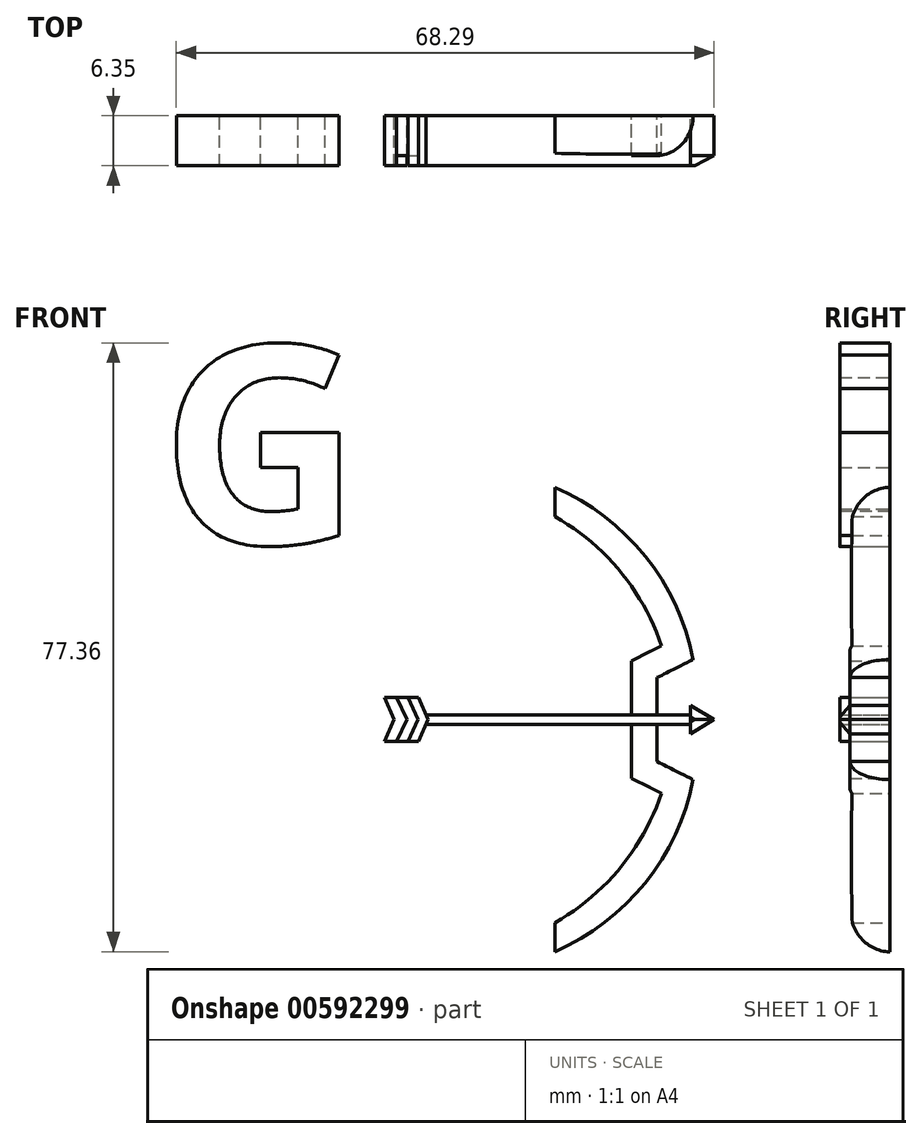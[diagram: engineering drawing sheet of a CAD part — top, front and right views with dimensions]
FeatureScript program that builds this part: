
annotation { "Feature Type Name" : "Feature", "Feature Type Description" : "" }
export const myFeature = defineFeature(function(context is Context, id is Id, definition is map)
    precondition{}
    {
        {
            var Q0;
            Q0=qCreatedBy(makeId("Front.planeOp"),FACE);
            var sketch = newSketch(context, id + "F0", { "sketchPlane" : qUnion([Q0])});
            skText(sketch, "E0", { "text": "G", "fontName": "OpenSans-Bold.ttf"});
            skArc(sketch, "E1", {"start": v(24.9, 7.63) * mm, "mid": v(18.82, 20.73) * mm, "end": v(7.34, 29.5) * mm});
            skLineSegment(sketch, "E2", {"start": v(24.9, 7.63) * mm, "end": v(20.3, 5.32) * mm});
            skLineSegment(sketch, "E3", {"start": v(20.3, 5.32) * mm, "end": v(20.3, 0.62) * mm});
            skArc(sketch, "E4", {"start": v(20.87, 9.35) * mm, "mid": v(15.63, 18.83) * mm, "end": v(7.34, 25.8) * mm});
            skLineSegment(sketch, "E5", {"start": v(7.34, 25.8) * mm, "end": v(-10.9, 2.79) * mm});
            skLineSegment(sketch, "E6", {"start": v(7.34, 29.5) * mm, "end": v(7.34, 25.8) * mm});
            skLineSegment(sketch, "E7", {"start": v(20.87, 9.35) * mm, "end": v(17.07, 7.46) * mm});
            skLineSegment(sketch, "E8", {"start": v(17.07, 7.46) * mm, "end": v(17.07, 0.62) * mm});
            skLineSegment(sketch, "E9.MirrorCS", {"start": v(20.3, -5.32) * mm, "end": v(20.3, -0.62) * mm});
            skLineSegment(sketch, "E10.MirrorCS", {"start": v(17.07, -7.46) * mm, "end": v(17.07, -0.62) * mm});
            skLineSegment(sketch, "E11.MirrorCS", {"start": v(20.87, -9.35) * mm, "end": v(17.07, -7.46) * mm});
            skLineSegment(sketch, "E12.MirrorCS", {"start": v(24.9, -7.63) * mm, "end": v(20.3, -5.32) * mm});
            skArc(sketch, "E13.MirrorCS", {"start": v(24.9, -7.63) * mm, "mid": v(18.82, -20.73) * mm, "end": v(7.34, -29.5) * mm});
            skArc(sketch, "E14.MirrorCS", {"start": v(20.87, -9.35) * mm, "mid": v(15.63, -18.83) * mm, "end": v(7.34, -25.8) * mm});
            skLineSegment(sketch, "E15.MirrorCS", {"start": v(7.34, -29.5) * mm, "end": v(7.34, -25.8) * mm});
            skLineSegment(sketch, "E16.MirrorCS", {"start": v(7.34, -25.8) * mm, "end": v(-10.9, -2.79) * mm});
            skLineSegment(sketch, "E17", {"start": v(-14.33, 2.79) * mm, "end": v(-13.11, 0) * mm});
            skLineSegment(sketch, "E18", {"start": v(-13.11, 0) * mm, "end": v(-8.8, 0) * mm});
            skLineSegment(sketch, "E19", {"start": v(-8.8, 0) * mm, "end": v(-10.01, 2.79) * mm});
            skLineSegment(sketch, "E20", {"start": v(-14.33, 2.79) * mm, "end": v(-10.01, 2.79) * mm});
            skLineSegment(sketch, "E21", {"start": v(-9.06, 0.62) * mm, "end": v(24.54, 0.62) * mm});
            skLineSegment(sketch, "E22", {"start": v(24.54, 0.62) * mm, "end": v(24.54, 1.82) * mm});
            skLineSegment(sketch, "E23", {"start": v(24.54, 1.82) * mm, "end": v(27.54, 0) * mm});
            skLineSegment(sketch, "E24", {"start": v(24.54, 0.62) * mm, "end": v(24.54, 0) * mm});
            skLineSegment(sketch, "E25", {"start": v(-11.33, 2.79) * mm, "end": v(-10.04, 0) * mm});
            skLineSegment(sketch, "E26", {"start": v(-12.8, 2.79) * mm, "end": v(-11.48, 0) * mm});
            skLineSegment(sketch, "E27.MirrorCS", {"start": v(-14.33, -2.79) * mm, "end": v(-13.11, 0) * mm});
            skLineSegment(sketch, "E28.MirrorCS", {"start": v(-14.33, -2.79) * mm, "end": v(-10.01, -2.79) * mm});
            skLineSegment(sketch, "E29.MirrorCS", {"start": v(-12.8, -2.79) * mm, "end": v(-11.48, 0) * mm});
            skLineSegment(sketch, "E30.MirrorCS", {"start": v(-11.33, -2.79) * mm, "end": v(-10.04, 0) * mm});
            skLineSegment(sketch, "E31.MirrorCS", {"start": v(-8.8, 0) * mm, "end": v(-10.01, -2.79) * mm});
            skLineSegment(sketch, "E32.MirrorCS", {"start": v(-9.06, -0.62) * mm, "end": v(24.54, -0.62) * mm});
            skLineSegment(sketch, "E33.MirrorCS", {"start": v(24.54, -1.82) * mm, "end": v(27.54, 0) * mm});
            skLineSegment(sketch, "E34.MirrorCS", {"start": v(24.54, -0.62) * mm, "end": v(24.54, -1.82) * mm});
            skLineSegment(sketch, "E35.MirrorCS", {"start": v(24.54, -0.62) * mm, "end": v(24.54, 0) * mm});
            skPoint(sketch, "E36.orphan", {"position": v(17.07, 0) * mm});
            skPoint(sketch, "E37.orphan", {"position": v(20.3, 0) * mm});
            skPoint(sketch, "E38.orphan", {"position": v(-13.11, 0) * mm});
            const initialGuessF0  = {"E0": [-0.0428, 0.02232, 1, 0, 0.0254]};
            skSetInitialGuess(sketch, initialGuessF0);
            skSolve(sketch);
        }
        {
            var Q0;
            Q0=makeQuery(id+"F0.imprint","IMPRINT",FACE,{"disambiguationData":[TD([[makeQuery(id+"F0.imprint","IMPRINT",EDGE,{"derivedFrom":sQuery(id+"F0.wireOp",EDGE,"E1")}),1.0]])]});
            var Q1;
            {var subQ1=sQuery(id+"F0.wireOp",EDGE,"E9.MirrorCS");Q1=makeQuery(id+"F0.imprint","IMPRINT",FACE,{"disambiguationData":[TD([[makeQuery(id+"F0.imprint","IMPRINT",EDGE,{"derivedFrom":subQ1}),1.0]])]});}
            var Q2;
            Q2=sQuery(id+"F0.wireOp",EDGE,"E5");
            var Q3;
            Q3=sQuery(id+"F0.wireOp",EDGE,"E16.MirrorCS");
            extrude(context, id + "F1", {"entities" : qUnion([Q0, Q1]), "bodyType" : ToolBodyType.SURFACE, "surfaceEntities" : qUnion([Q2, Q3]), "depth" : 5.08 * mm, "offsetDistance" : 25.4 * mm});
        }
        {
            var Q0;
            Q0=makeQuery(id+"F0.imprint","IMPRINT",FACE,{"disambiguationData":[TD([[makeQuery(id+"F0.imprint","IMPRINT",EDGE,{"derivedFrom":sQuery(id+"F0.wireOp",EDGE,"E1")}),1.0]])]});
            var Q1;
            {var subQ1=sQuery(id+"F0.wireOp",EDGE,"E9.MirrorCS");Q1=makeQuery(id+"F0.imprint","IMPRINT",FACE,{"disambiguationData":[TD([[makeQuery(id+"F0.imprint","IMPRINT",EDGE,{"derivedFrom":subQ1}),1.0]])]});}
            var Q2;
            {var subQ0=sQuery(id+"F0.wireOp",EDGE,"E25");Q2=makeQuery(id+"F0.imprint","IMPRINT",FACE,{"disambiguationData":[TD([[makeQuery(id+"F0.imprint","IMPRINT",EDGE,{"derivedFrom":subQ0}),-1.0]])]});}
            var Q3;
            {var subQ2=sQuery(id+"F0.wireOp",EDGE,"E29.MirrorCS");Q3=makeQuery(id+"F0.imprint","IMPRINT",FACE,{"disambiguationData":[TD([[makeQuery(id+"F0.imprint","IMPRINT",EDGE,{"derivedFrom":subQ2}),-1.0]])]});}
            extrude(context, id + "F2", {"entities" : qUnion([Q0, Q1, Q2, Q3]), "depth" : 5.08 * mm, "offsetDistance" : 25.4 * mm});
        }
        {
            var Q0;
            {var subQ2=sQuery(id+"F0.wireOp",EDGE,"E24");Q0=makeQuery(id+"F0.imprint","IMPRINT",FACE,{"disambiguationData":[TD([[makeQuery(id+"F0.imprint","IMPRINT",EDGE,{"derivedFrom":subQ2}),-1.0]])]});}
            var Q1;
            {var subQ0=sQuery(id+"F0.wireOp",EDGE,"E17");Q1=makeQuery(id+"F0.imprint","IMPRINT",FACE,{"disambiguationData":[TD([[makeQuery(id+"F0.imprint","IMPRINT",EDGE,{"derivedFrom":subQ0}),1.0]])]});}
            var Q2;
            {var subQ4=sQuery(id+"F0.wireOp",EDGE,"E25");Q2=makeQuery(id+"F0.imprint","IMPRINT",FACE,{"disambiguationData":[TD([[makeQuery(id+"F0.imprint","IMPRINT",EDGE,{"derivedFrom":subQ4}),1.0]])]});}
            var Q3;
            {var subQ0=sQuery(id+"F0.wireOp",EDGE,"E27.MirrorCS");Q3=makeQuery(id+"F0.imprint","IMPRINT",FACE,{"disambiguationData":[TD([[makeQuery(id+"F0.imprint","IMPRINT",EDGE,{"derivedFrom":subQ0}),-1.0]])]});}
            var Q4;
            {var subQ0=sQuery(id+"F0.wireOp",EDGE,"E30.MirrorCS");Q4=makeQuery(id+"F0.imprint","IMPRINT",FACE,{"disambiguationData":[TD([[makeQuery(id+"F0.imprint","IMPRINT",EDGE,{"derivedFrom":subQ0}),-1.0]])]});}
            var Q5;
            Q5=makeQuery(id+"F0.imprint","IMPRINT",FACE,{"disambiguationData":[TD([[makeQuery(id+"F0.imprint","IMPRINT",EDGE,{"derivedFrom":sQuery(id+"F0.wireOp",EDGE,"E0.sketch_text.stroke-0")}),-1.0]])]});
            var Q6;
            Q6=makeQuery(id+"F0.imprint","IMPRINT",FACE,{"disambiguationData":[TD([[makeQuery(id+"F0.imprint","IMPRINT",EDGE,{"derivedFrom":sQuery(id+"F0.wireOp",EDGE,"E22")}),-1.0]])]});
            extrude(context, id + "F3", {"entities" : qUnion([Q0, Q1, Q2, Q3, Q4, Q5, Q6]), "depth" : 6.35 * mm, "offsetDistance" : 25.4 * mm});
        }
        {
            var Q0;
            Q0=makeQuery(id+"F3.opExtrude","CAP_EDGE",EDGE,{"disambiguationData":[OSD([sQuery(id+"F0.wireOp",EDGE,"E32.MirrorCS")])],"isStart":false});
            var Q1;
            Q1=makeQuery(id+"F3.opExtrude","CAP_EDGE",EDGE,{"disambiguationData":[OSD([sQuery(id+"F0.wireOp",EDGE,"E21")])],"isStart":false});
            fillet(context, id + "F4", {"entities" : qUnion([Q0, Q1]), "radius" : 0.6 * mm, "tangentPropagation" : true, "allowEdgeOverflow" : false});
        }
        {
            var Q0;
            Q0=makeQuery(id+"F2.opExtrude","CAP_EDGE",EDGE,{"disambiguationData":[OSD([sQuery(id+"F0.wireOp",EDGE,"E1")])],"isStart":false});
            var Q1;
            Q1=makeQuery(id+"F2.opExtrude","CAP_EDGE",EDGE,{"disambiguationData":[OSD([sQuery(id+"F0.wireOp",EDGE,"E13.MirrorCS")])],"isStart":false});
            fillet(context, id + "F5", {"entities" : qUnion([Q0, Q1]), "radius" : 5.08 * mm, "tangentPropagation" : true, "allowEdgeOverflow" : false});
        }
        {
            var Q0;
            Q0=makeQuery(id+"F3.opExtrude","CAP_EDGE",EDGE,{"disambiguationData":[OSD([sQuery(id+"F0.wireOp",EDGE,"E33.MirrorCS")])],"isStart":false});
            var Q1;
            Q1=makeQuery(id+"F3.opExtrude","CAP_EDGE",EDGE,{"disambiguationData":[OSD([sQuery(id+"F0.wireOp",EDGE,"E23")])],"isStart":false});
            chamfer(context, id + "F6", {"entities" : qUnion([Q0, Q1]), "width" : 1.27 * mm, "tangentPropagation" : true});
        }
    });
